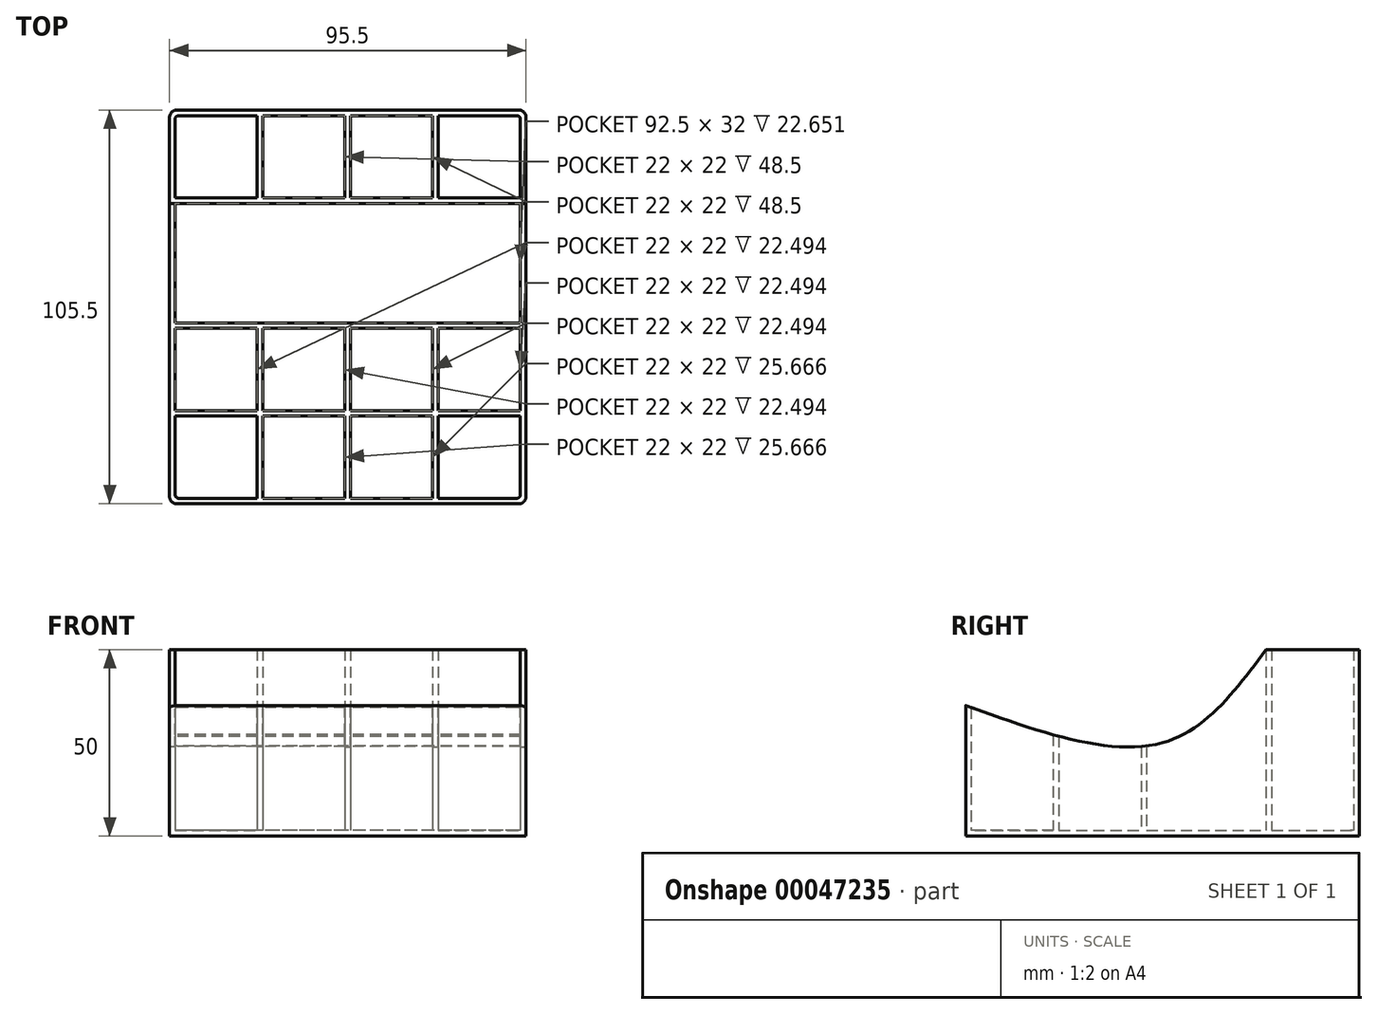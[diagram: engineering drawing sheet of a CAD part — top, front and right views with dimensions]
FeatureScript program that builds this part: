
annotation { "Feature Type Name" : "Feature", "Feature Type Description" : "" }
export const myFeature = defineFeature(function(context is Context, id is Id, definition is map)
    precondition{}
    {
        {
            var Q0;
            Q0=qCreatedBy(makeId("Top.planeOp"),FACE);
            var sketch = newSketch(context, id + "F0", { "sketchPlane" : qUnion([Q0])});
            skLineSegment(sketch, "E0", {"start": v(0, 0) * mm, "end": v(22, 0) * mm});
            skLineSegment(sketch, "E1", {"start": v(0, 0) * mm, "end": v(0, 22) * mm});
            skLineSegment(sketch, "E2", {"start": v(0, 22) * mm, "end": v(22, 22) * mm});
            skLineSegment(sketch, "E3", {"start": v(22, 22) * mm, "end": v(22, 0) * mm});
            skLineSegment(sketch, "E4.0.1.0", {"start": v(0, 23.5) * mm, "end": v(0, 45.5) * mm});
            skLineSegment(sketch, "E4.0.1.1", {"start": v(0, 45.5) * mm, "end": v(22, 45.5) * mm});
            skLineSegment(sketch, "E4.0.1.2", {"start": v(0, 23.5) * mm, "end": v(22, 23.5) * mm});
            skLineSegment(sketch, "E4.0.1.3", {"start": v(22, 45.5) * mm, "end": v(22, 23.5) * mm});
            skLineSegment(sketch, "E4.1.0.0", {"start": v(23.5, 0) * mm, "end": v(23.5, 22) * mm});
            skLineSegment(sketch, "E4.1.0.1", {"start": v(23.5, 22) * mm, "end": v(45.5, 22) * mm});
            skLineSegment(sketch, "E4.1.0.2", {"start": v(23.5, 0) * mm, "end": v(45.5, 0) * mm});
            skLineSegment(sketch, "E4.1.0.3", {"start": v(45.5, 22) * mm, "end": v(45.5, 0) * mm});
            skLineSegment(sketch, "E4.1.1.0", {"start": v(23.5, 23.5) * mm, "end": v(23.5, 45.5) * mm});
            skLineSegment(sketch, "E4.1.1.1", {"start": v(23.5, 45.5) * mm, "end": v(45.5, 45.5) * mm});
            skLineSegment(sketch, "E4.1.1.2", {"start": v(23.5, 23.5) * mm, "end": v(45.5, 23.5) * mm});
            skLineSegment(sketch, "E4.1.1.3", {"start": v(45.5, 45.5) * mm, "end": v(45.5, 23.5) * mm});
            skLineSegment(sketch, "E4.2.0.0", {"start": v(47, 0) * mm, "end": v(47, 22) * mm});
            skLineSegment(sketch, "E4.2.0.1", {"start": v(47, 22) * mm, "end": v(69, 22) * mm});
            skLineSegment(sketch, "E4.2.0.2", {"start": v(47, 0) * mm, "end": v(69, 0) * mm});
            skLineSegment(sketch, "E4.2.0.3", {"start": v(69, 22) * mm, "end": v(69, 0) * mm});
            skLineSegment(sketch, "E4.2.1.0", {"start": v(47, 23.5) * mm, "end": v(47, 45.5) * mm});
            skLineSegment(sketch, "E4.2.1.1", {"start": v(47, 45.5) * mm, "end": v(69, 45.5) * mm});
            skLineSegment(sketch, "E4.2.1.2", {"start": v(47, 23.5) * mm, "end": v(69, 23.5) * mm});
            skLineSegment(sketch, "E4.2.1.3", {"start": v(69, 45.5) * mm, "end": v(69, 23.5) * mm});
            skLineSegment(sketch, "E4.3.0.0", {"start": v(70.5, 0) * mm, "end": v(70.5, 22) * mm});
            skLineSegment(sketch, "E4.3.0.1", {"start": v(70.5, 22) * mm, "end": v(92.5, 22) * mm});
            skLineSegment(sketch, "E4.3.0.2", {"start": v(70.5, 0) * mm, "end": v(92.5, 0) * mm});
            skLineSegment(sketch, "E4.3.0.3", {"start": v(92.5, 22) * mm, "end": v(92.5, 0) * mm});
            skLineSegment(sketch, "E4.3.1.0", {"start": v(70.5, 23.5) * mm, "end": v(70.5, 45.5) * mm});
            skLineSegment(sketch, "E4.3.1.1", {"start": v(70.5, 45.5) * mm, "end": v(92.5, 45.5) * mm});
            skLineSegment(sketch, "E4.3.1.2", {"start": v(70.5, 23.5) * mm, "end": v(92.5, 23.5) * mm});
            skLineSegment(sketch, "E4.3.1.3", {"start": v(92.5, 45.5) * mm, "end": v(92.5, 23.5) * mm});
            skLineSegment(sketch, "E4.direction1", {"start": v(0, 0) * mm, "end": v(23.5, 0) * mm, "construction": true});
            skLineSegment(sketch, "E4.direction2", {"start": v(0, 0) * mm, "end": v(0, 23.5) * mm, "construction": true});
            skLineSegment(sketch, "E5", {"start": v(0, 45.5) * mm, "end": v(0, 47) * mm});
            skLineSegment(sketch, "E6", {"start": v(0, 47) * mm, "end": v(0, 79) * mm});
            skLineSegment(sketch, "E7", {"start": v(0, 79) * mm, "end": v(92.5, 79) * mm});
            skLineSegment(sketch, "E8", {"start": v(92.5, 79) * mm, "end": v(92.5, 47) * mm});
            skLineSegment(sketch, "E9", {"start": v(92.5, 47) * mm, "end": v(0, 47) * mm});
            skLineSegment(sketch, "E10", {"start": v(0, 79) * mm, "end": v(0, 80.5) * mm});
            skLineSegment(sketch, "E11", {"start": v(0, 80.5) * mm, "end": v(22, 80.5) * mm});
            skLineSegment(sketch, "E12", {"start": v(22, 80.5) * mm, "end": v(22, 102.5) * mm});
            skLineSegment(sketch, "E13", {"start": v(22, 102.5) * mm, "end": v(0, 102.5) * mm});
            skLineSegment(sketch, "E14", {"start": v(0, 102.5) * mm, "end": v(0, 80.5) * mm});
            skLineSegment(sketch, "E15.1.0.0", {"start": v(45.5, 102.5) * mm, "end": v(23.5, 102.5) * mm});
            skLineSegment(sketch, "E15.1.0.1", {"start": v(23.5, 102.5) * mm, "end": v(23.5, 80.5) * mm});
            skLineSegment(sketch, "E15.1.0.2", {"start": v(23.5, 80.5) * mm, "end": v(45.5, 80.5) * mm});
            skLineSegment(sketch, "E15.1.0.3", {"start": v(45.5, 80.5) * mm, "end": v(45.5, 102.5) * mm});
            skLineSegment(sketch, "E15.2.0.0", {"start": v(69, 102.5) * mm, "end": v(47, 102.5) * mm});
            skLineSegment(sketch, "E15.2.0.1", {"start": v(47, 102.5) * mm, "end": v(47, 80.5) * mm});
            skLineSegment(sketch, "E15.2.0.2", {"start": v(47, 80.5) * mm, "end": v(69, 80.5) * mm});
            skLineSegment(sketch, "E15.2.0.3", {"start": v(69, 80.5) * mm, "end": v(69, 102.5) * mm});
            skLineSegment(sketch, "E15.3.0.0", {"start": v(92.5, 102.5) * mm, "end": v(70.5, 102.5) * mm});
            skLineSegment(sketch, "E15.3.0.1", {"start": v(70.5, 102.5) * mm, "end": v(70.5, 80.5) * mm});
            skLineSegment(sketch, "E15.3.0.2", {"start": v(70.5, 80.5) * mm, "end": v(92.5, 80.5) * mm});
            skLineSegment(sketch, "E15.3.0.3", {"start": v(92.5, 80.5) * mm, "end": v(92.5, 102.5) * mm});
            skLineSegment(sketch, "E15.direction1", {"start": v(0, 102.5) * mm, "end": v(23.5, 102.5) * mm, "construction": true});
            skLineSegment(sketch, "E16", {"start": v(-1.5, -1.5) * mm, "end": v(94, -1.5) * mm});
            skLineSegment(sketch, "E17", {"start": v(94, -1.5) * mm, "end": v(94, 104) * mm});
            skLineSegment(sketch, "E18", {"start": v(94, 104) * mm, "end": v(-1.5, 104) * mm});
            skLineSegment(sketch, "E19", {"start": v(-1.5, 104) * mm, "end": v(-1.5, -1.5) * mm});
            skSolve(sketch);
        }
        {
            var Q0;
            Q0 = qSketchRegion(id + "F0", true);
            extrude(context, id + "F1", {"entities" : qUnion([Q0]), "depth" : 50 * mm});
        }
        {
            var Q0;
            Q0=qCreatedBy(makeId("Top.planeOp"),FACE);
            var sketch = newSketch(context, id + "F2", { "sketchPlane" : qUnion([Q0])});
            skLineSegment(sketch, "E20.0", {"start": v(-1.5, -1.5) * mm, "end": v(94, -1.5) * mm});
            skLineSegment(sketch, "E20.1", {"start": v(-1.5, 104) * mm, "end": v(-1.5, -1.5) * mm});
            skLineSegment(sketch, "E20.2", {"start": v(94, 104) * mm, "end": v(-1.5, 104) * mm});
            skLineSegment(sketch, "E20.3", {"start": v(94, -1.5) * mm, "end": v(94, 104) * mm});
            skSolve(sketch);
        }
        {
            var Q0;
            Q0=makeQuery(id+"F2.imprint","IMPRINT",FACE,{"disambiguationData":[TD([[makeQuery(id+"F2.imprint","IMPRINT",EDGE,{"derivedFrom":sQuery(id+"F2.wireOp",EDGE,"E20.0")}),1.0]])]});
            extrude(context, id + "F3", {"entities" : qUnion([Q0]), "operationType" : NewBodyOperationType.ADD, "depth" : 1.5 * mm});
        }
        {
            var Q0;
            Q0=makeQuery(id+"F1.opExtrude","SWEPT_FACE",FACE,{"disambiguationData":[OSD([sQuery(id+"F0.wireOp",EDGE,"E19")])]});
            var sketch = newSketch(context, id + "F4", { "sketchPlane" : qUnion([Q0])});
            skLineSegment(sketch, "E21", {"start": v(-104, 50) * mm, "end": v(-79, 50) * mm});
            skLineSegment(sketch, "E22", {"start": v(-51.25, 0) * mm, "end": v(-51.25, 25) * mm});
            skLineSegment(sketch, "E23", {"start": v(1.5, 0) * mm, "end": v(1.5, 35) * mm});
            skFitSpline(sketch, "E24", {"points": [v(-79, 50) * mm, v(-51.25, 25) * mm, v(1.5, 35) * mm], "startDerivative": vector(52.9, -71.64) * mm, "endDerivative": vector(106.49, 38.33) * mm});
            skLineSegment(sketch, "E25", {"start": v(-79, 50) * mm, "end": v(1.5, 50) * mm});
            skLineSegment(sketch, "E26", {"start": v(1.5, 50) * mm, "end": v(1.5, 35) * mm});
            skSolve(sketch);
        }
        {
            var Q0;
            {var subQ3=sQuery(id+"F4.wireOp",EDGE,"E25");Q0=makeQuery(id+"F4.imprint","IMPRINT",FACE,{"disambiguationData":[TD([[makeQuery(id+"F4.imprint","IMPRINT",EDGE,{"derivedFrom":subQ3}),-1.0]])]});}
            extrude(context, id + "F5", {"entities" : qUnion([Q0]), "operationType" : NewBodyOperationType.REMOVE, "oppositeDirection" : true, "depth" : 100 * mm});
        }
        {
            var Q0;
            Q0=makeQuery(id+"F1.opExtrude","SWEPT_EDGE",EDGE,{"disambiguationData":[OSD([sQuery(id+"F0.wireOp",EDGE,"E16"),sQuery(id+"F0.wireOp",EDGE,"E17")])]});
            var Q1;
            Q1=makeQuery(id+"F1.opExtrude","SWEPT_EDGE",EDGE,{"disambiguationData":[OSD([sQuery(id+"F0.wireOp",EDGE,"E17"),sQuery(id+"F0.wireOp",EDGE,"E18")])]});
            var Q2;
            Q2=makeQuery(id+"F1.opExtrude","SWEPT_EDGE",EDGE,{"disambiguationData":[OSD([sQuery(id+"F0.wireOp",EDGE,"E16"),sQuery(id+"F0.wireOp",EDGE,"E19")])]});
            var Q3;
            Q3=makeQuery(id+"F1.opExtrude","SWEPT_EDGE",EDGE,{"disambiguationData":[OSD([sQuery(id+"F0.wireOp",EDGE,"E18"),sQuery(id+"F0.wireOp",EDGE,"E19")])]});
            fillet(context, id + "F6", {"entities" : qUnion([Q0, Q1, Q2, Q3]), "radius" : 2 * mm, "tangentPropagation" : true, "allowEdgeOverflow" : false});
        }
        {
            var Q0;
            Q0=makeQuery(id+"F1.opExtrude","SWEPT_EDGE",EDGE,{"disambiguationData":[OSD([sQuery(id+"F0.wireOp",EDGE,"E0"),sQuery(id+"F0.wireOp",EDGE,"E1")])]});
            var Q1;
            Q1=makeQuery(id+"F1.opExtrude","SWEPT_EDGE",EDGE,{"disambiguationData":[OSD([sQuery(id+"F0.wireOp",EDGE,"E4.3.0.2"),sQuery(id+"F0.wireOp",EDGE,"E4.3.0.3")])]});
            var Q2;
            Q2=makeQuery(id+"F1.opExtrude","SWEPT_EDGE",EDGE,{"disambiguationData":[OSD([sQuery(id+"F0.wireOp",EDGE,"E15.3.0.0"),sQuery(id+"F0.wireOp",EDGE,"E15.3.0.3")])]});
            var Q3;
            Q3=makeQuery(id+"F1.opExtrude","SWEPT_EDGE",EDGE,{"disambiguationData":[OSD([sQuery(id+"F0.wireOp",EDGE,"E13"),sQuery(id+"F0.wireOp",EDGE,"E14")])]});
            fillet(context, id + "F7", {"entities" : qUnion([Q0, Q1, Q2, Q3]), "radius" : 1 * mm, "tangentPropagation" : true, "allowEdgeOverflow" : false});
        }
    });
